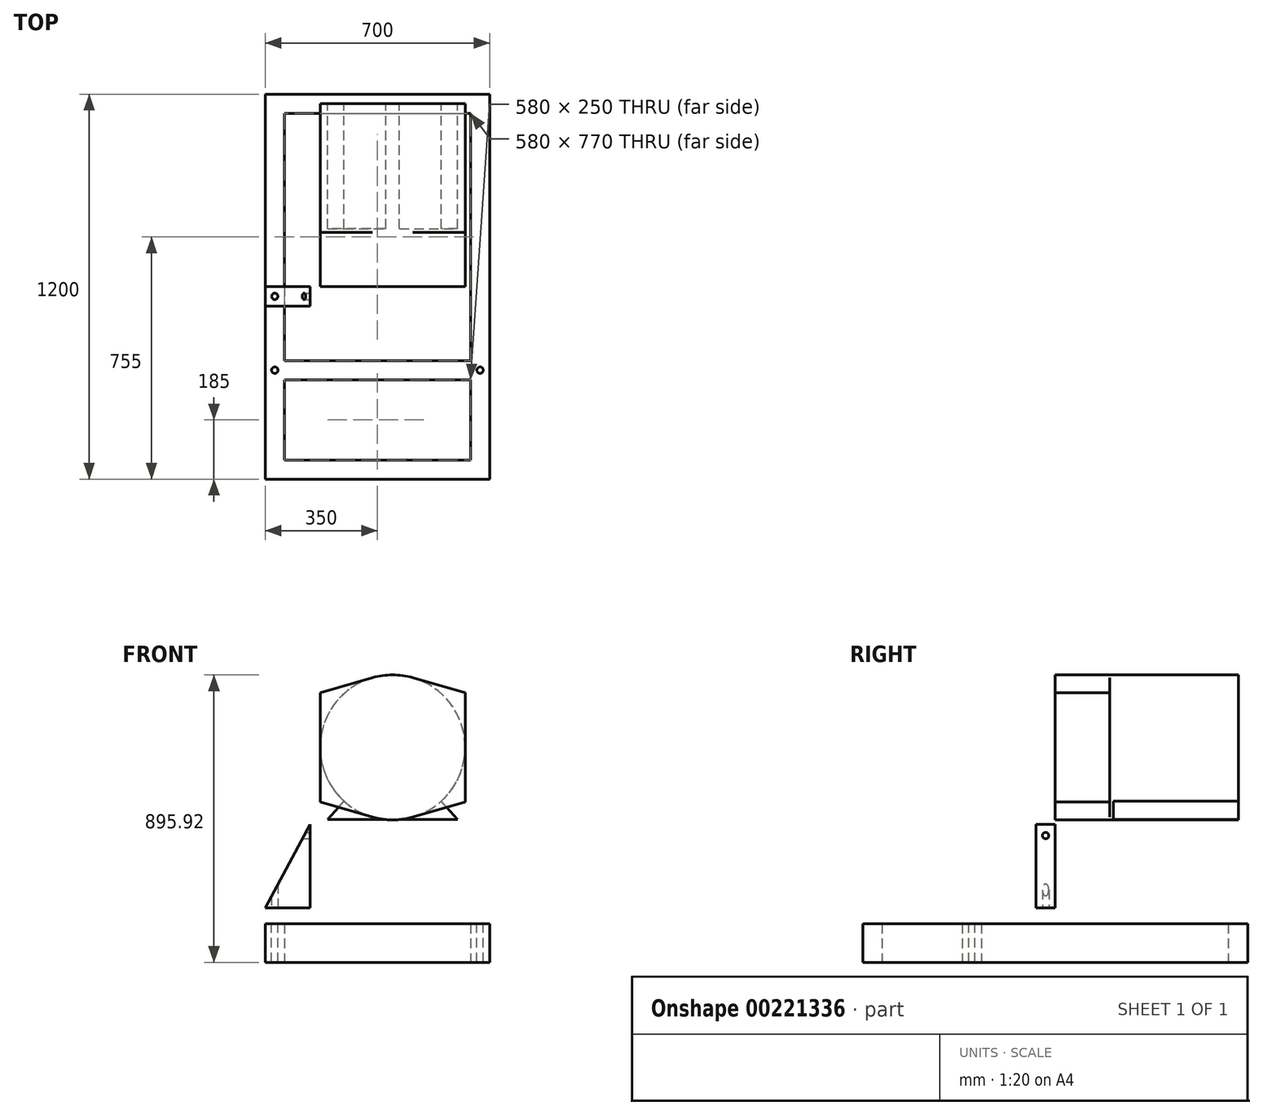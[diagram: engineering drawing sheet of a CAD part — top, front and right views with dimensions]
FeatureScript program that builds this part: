
annotation { "Feature Type Name" : "Feature", "Feature Type Description" : "" }
export const myFeature = defineFeature(function(context is Context, id is Id, definition is map)
    precondition{}
    {
        {
            var Q0;
            Q0=qCreatedBy(makeId("Top.planeOp"),FACE);
            var sketch = newSketch(context, id + "F0", { "sketchPlane" : qUnion([Q0])});
            skLineSegment(sketch, "E0.bottom", {"start": v(-300, 600) * mm, "end": v(400, 600) * mm});
            skLineSegment(sketch, "E0.top", {"start": v(-300, -600) * mm, "end": v(400, -600) * mm});
            skLineSegment(sketch, "E0.left", {"start": v(-300, 600) * mm, "end": v(-300, -600) * mm});
            skLineSegment(sketch, "E0.right", {"start": v(400, 600) * mm, "end": v(400, -600) * mm});
            skLineSegment(sketch, "E1.bottom", {"start": v(-240, 540) * mm, "end": v(340, 540) * mm});
            skLineSegment(sketch, "E1.top", {"start": v(-240, -540) * mm, "end": v(340, -540) * mm});
            skLineSegment(sketch, "E1.left", {"start": v(-240, 540) * mm, "end": v(-240, -540) * mm});
            skLineSegment(sketch, "E1.right", {"start": v(340, 540) * mm, "end": v(340, -540) * mm});
            skLineSegment(sketch, "E2", {"start": v(-240, -290) * mm, "end": v(340, -290) * mm});
            skLineSegment(sketch, "E3.0", {"start": v(-240, -230) * mm, "end": v(340, -230) * mm});
            skSolve(sketch);
        }
        {
            var Q0;
            Q0=makeQuery(id+"F0.imprint","IMPRINT",FACE,{"disambiguationData":[TD([[makeQuery(id+"F0.imprint","IMPRINT",EDGE,{"derivedFrom":sQuery(id+"F0.wireOp",EDGE,"E0.bottom")}),-1.0]])]});
            extrude(context, id + "F1", {"entities" : qUnion([Q0]), "depth" : 120 * mm});
        }
        {
            var Q0;
            {var subQ0=sQuery(id+"F0.wireOp",EDGE,"E2");Q0=makeQuery(id+"F0.imprint","IMPRINT",FACE,{"disambiguationData":[TD([[makeQuery(id+"F0.imprint","IMPRINT",EDGE,{"derivedFrom":subQ0}),1.0]])]});}
            extrude(context, id + "F2", {"entities" : qUnion([Q0]), "operationType" : NewBodyOperationType.ADD, "depth" : 120 * mm});
        }
        {
            var Q0;
            Q0=qCreatedBy(makeId("Front.planeOp"),FACE);
            var sketch = newSketch(context, id + "F3", { "sketchPlane" : qUnion([Q0])});
            skLineSegment(sketch, "E4", {"start": v(-160, 170) * mm, "end": v(-160, 430) * mm});
            skLineSegment(sketch, "E5", {"start": v(-160, 430) * mm, "end": v(-300, 170) * mm});
            skLineSegment(sketch, "E6", {"start": v(-300, 170) * mm, "end": v(-160, 170) * mm});
            skSolve(sketch);
        }
        {
            var Q0;
            Q0=makeQuery(id+"F3.imprint","IMPRINT",FACE,{"disambiguationData":[TD([[makeQuery(id+"F3.imprint","IMPRINT",EDGE,{"derivedFrom":sQuery(id+"F3.wireOp",EDGE,"E4")}),1.0]])]});
            extrude(context, id + "F4", {"entities" : qUnion([Q0]), "depth" : 60 * mm});
        }
        {
            var Q0;
            {var subQ0=sQuery(id+"F0.wireOp",EDGE,"E1.right");var subQ1=sQuery(id+"F0.wireOp",EDGE,"E1.left");Q0=makeQuery(id+"F2.boolean.opBoolean","MERGE",FACE,{"derivedFrom":[makeQuery(id+"F1.opExtrude","CAP_FACE",FACE,{"disambiguationData":[OSD([sQuery(id+"F0.wireOp",EDGE,"E0.bottom"),sQuery(id+"F0.wireOp",EDGE,"E0.top"),sQuery(id+"F0.wireOp",EDGE,"E0.left"),sQuery(id+"F0.wireOp",EDGE,"E0.right"),sQuery(id+"F0.wireOp",EDGE,"E1.bottom"),sQuery(id+"F0.wireOp",EDGE,"E1.top"),subQ1,subQ0])],"isStart":false}),makeQuery(id+"F2.opExtrude","CAP_FACE",FACE,{"disambiguationData":[OSD([subQ1,subQ0,sQuery(id+"F0.wireOp",EDGE,"E2"),sQuery(id+"F0.wireOp",EDGE,"E3.0")])],"isStart":false})]});}
            var sketch = newSketch(context, id + "F5", { "sketchPlane" : qUnion([Q0])});
            skCircle(sketch, "E7", {"center": v(-270, -260) * mm, "radius": 10 * mm});
            skCircle(sketch, "E8", {"center": v(370, -260) * mm, "radius": 10 * mm});
            skSolve(sketch);
        }
        {
            var Q0;
            Q0=makeQuery(id+"F5.imprint","IMPRINT",FACE,{"disambiguationData":[TD([[makeQuery(id+"F5.imprint","IMPRINT",EDGE,{"derivedFrom":sQuery(id+"F5.wireOp",EDGE,"E7")}),1.0]])]});
            var Q1;
            Q1=makeQuery(id+"F5.imprint","IMPRINT",FACE,{"disambiguationData":[TD([[makeQuery(id+"F5.imprint","IMPRINT",EDGE,{"derivedFrom":sQuery(id+"F5.wireOp",EDGE,"E8")}),1.0]])]});
            var Q2;
            Q2=sQuery(id+"F5.wireOp",EDGE,"E7");
            extrude(context, id + "F6", {"entities" : qUnion([Q0, Q1]), "operationType" : NewBodyOperationType.REMOVE, "surfaceEntities" : qUnion([Q2]), "oppositeDirection" : true, "depth" : 200 * mm});
        }
        {
            var Q0;
            Q0=makeQuery(id+"F4.opExtrude","SWEPT_FACE",FACE,{"disambiguationData":[OSD([sQuery(id+"F3.wireOp",EDGE,"E6")])]});
            var sketch = newSketch(context, id + "F7", { "sketchPlane" : qUnion([Q0])});
            skCircle(sketch, "E9", {"center": v(-270, 30) * mm, "radius": 10 * mm});
            skSolve(sketch);
        }
        {
            var Q0;
            Q0=makeQuery(id+"F7.imprint","IMPRINT",FACE,{"disambiguationData":[TD([[makeQuery(id+"F7.imprint","IMPRINT",EDGE,{"derivedFrom":sQuery(id+"F7.wireOp",EDGE,"E9")}),1.0]])]});
            extrude(context, id + "F8", {"entities" : qUnion([Q0]), "operationType" : NewBodyOperationType.REMOVE, "oppositeDirection" : true, "depth" : 100 * mm});
        }
        {
            var Q0;
            Q0=makeQuery(id+"F4.opExtrude","SWEPT_FACE",FACE,{"disambiguationData":[OSD([sQuery(id+"F3.wireOp",EDGE,"E4")])]});
            var sketch = newSketch(context, id + "F9", { "sketchPlane" : qUnion([Q0])});
            skCircle(sketch, "E10", {"center": v(-30, 395) * mm, "radius": 10 * mm});
            skSolve(sketch);
        }
        {
            var Q0;
            Q0=makeQuery(id+"F9.imprint","IMPRINT",FACE,{"disambiguationData":[TD([[makeQuery(id+"F9.imprint","IMPRINT",EDGE,{"derivedFrom":sQuery(id+"F9.wireOp",EDGE,"E10")}),1.0]])]});
            extrude(context, id + "F10", {"entities" : qUnion([Q0]), "operationType" : NewBodyOperationType.REMOVE, "oppositeDirection" : true, "depth" : 50 * mm});
        }
        {
            var Q0;
            Q0=qCreatedBy(makeId("Front.planeOp"),FACE);
            var sketch = newSketch(context, id + "F11", { "sketchPlane" : qUnion([Q0])});
            skCircle(sketch, "E11", {"center": v(97.42, 669.92) * mm, "radius": 226 * mm});
            skSolve(sketch);
        }
        {
            var Q0;
            Q0=makeQuery(id+"F11.imprint","IMPRINT",FACE,{"disambiguationData":[TD([[makeQuery(id+"F11.imprint","IMPRINT",EDGE,{"derivedFrom":sQuery(id+"F11.wireOp",EDGE,"E11")}),1.0]])]});
            extrude(context, id + "F12", {"entities" : qUnion([Q0]), "oppositeDirection" : true, "depth" : 571 * mm});
        }
        {
            var Q0;
            Q0=makeQuery(id+"F12.opExtrude","CAP_FACE",FACE,{"disambiguationData":[OSD([sQuery(id+"F11.wireOp",EDGE,"E11")])],"isStart":true});
            var sketch = newSketch(context, id + "F13", { "sketchPlane" : qUnion([Q0])});
            skLineSegment(sketch, "E12", {"start": v(97.42, 669.92) * mm, "end": v(323.42, 669.92) * mm});
            skLineSegment(sketch, "E13", {"start": v(97.42, 669.92) * mm, "end": v(97.42, 443.92) * mm});
            skLineSegment(sketch, "E14", {"start": v(323.42, 499.92) * mm, "end": v(160.08, 452.78) * mm});
            skLineSegment(sketch, "E15", {"start": v(323.42, 499.92) * mm, "end": v(323.42, 669.92) * mm});
            skLineSegment(sketch, "E16.MirrorCS", {"start": v(323.42, 839.92) * mm, "end": v(323.42, 669.92) * mm});
            skLineSegment(sketch, "E17.MirrorCS", {"start": v(323.42, 839.92) * mm, "end": v(160.08, 887.06) * mm});
            skLineSegment(sketch, "E18.MirrorCS", {"start": v(-128.58, 839.92) * mm, "end": v(-128.58, 669.92) * mm});
            skLineSegment(sketch, "E19.MirrorCS", {"start": v(-128.58, 839.92) * mm, "end": v(34.75, 887.06) * mm});
            skLineSegment(sketch, "E20.MirrorCS", {"start": v(-128.58, 499.92) * mm, "end": v(-128.58, 669.92) * mm});
            skLineSegment(sketch, "E21.MirrorCS", {"start": v(-128.58, 499.92) * mm, "end": v(34.75, 452.78) * mm});
            skSolve(sketch);
        }
        {
            var Q0;
            {var subQ0=sQuery(id+"F13.wireOp",EDGE,"E14");Q0=makeQuery(id+"F13.imprint","IMPRINT",FACE,{"disambiguationData":[TD([[makeQuery(id+"F13.imprint","IMPRINT",EDGE,{"derivedFrom":subQ0}),-1.0]])]});}
            var Q1;
            {var subQ0=sQuery(id+"F13.wireOp",EDGE,"E16.MirrorCS");Q1=makeQuery(id+"F13.imprint","IMPRINT",FACE,{"disambiguationData":[TD([[makeQuery(id+"F13.imprint","IMPRINT",EDGE,{"derivedFrom":subQ0}),-1.0]])]});}
            var Q2;
            {var subQ0=sQuery(id+"F13.wireOp",EDGE,"E18.MirrorCS");Q2=makeQuery(id+"F13.imprint","IMPRINT",FACE,{"disambiguationData":[TD([[makeQuery(id+"F13.imprint","IMPRINT",EDGE,{"derivedFrom":subQ0}),1.0]])]});}
            var Q3;
            {var subQ0=sQuery(id+"F13.wireOp",EDGE,"E20.MirrorCS");Q3=makeQuery(id+"F13.imprint","IMPRINT",FACE,{"disambiguationData":[TD([[makeQuery(id+"F13.imprint","IMPRINT",EDGE,{"derivedFrom":subQ0}),-1.0]])]});}
            extrude(context, id + "F14", {"entities" : qUnion([Q0, Q1, Q2, Q3]), "operationType" : NewBodyOperationType.ADD, "oppositeDirection" : true, "depth" : 170 * mm});
        }
        {
            var Q0;
            Q0=makeQuery(id+"F12.opExtrude","CAP_FACE",FACE,{"disambiguationData":[OSD([sQuery(id+"F11.wireOp",EDGE,"E11")])],"isStart":false});
            var sketch = newSketch(context, id + "F15", { "sketchPlane" : qUnion([Q0])});
            skLineSegment(sketch, "E22", {"start": v(-97.42, 669.92) * mm, "end": v(-97.42, 444.92) * mm});
            skLineSegment(sketch, "E23", {"start": v(-97.42, 444.92) * mm, "end": v(-300.42, 444.92) * mm});
            skLineSegment(sketch, "E24", {"start": v(-300.42, 444.92) * mm, "end": v(-97.42, 669.92) * mm});
            skLineSegment(sketch, "E25.MirrorCS", {"start": v(-97.42, 444.92) * mm, "end": v(105.58, 444.92) * mm});
            skLineSegment(sketch, "E26.MirrorCS", {"start": v(105.58, 444.92) * mm, "end": v(-97.42, 669.92) * mm});
            skSolve(sketch);
        }
        {
            var Q0;
            {var subQ0=sQuery(id+"F15.wireOp",EDGE,"E24");var subQ1=sQuery(id+"F15.wireOp",EDGE,"E23");var subQ2=makeQuery(id+"F15.imprint","INTERSECT",VERTEX,{"derivedFrom":[subQ1,subQ0]});Q0=makeQuery(id+"F15.imprint","IMPRINT",FACE,{"disambiguationData":[TD([[makeQuery(id+"F15.imprint","IMPRINT",EDGE,{"disambiguationData":[TD([[subQ2,1.0]])],"derivedFrom":subQ1}),-1.0]])]});}
            var Q1;
            {var subQ0=sQuery(id+"F15.wireOp",EDGE,"E26.MirrorCS");var subQ1=sQuery(id+"F15.wireOp",EDGE,"E25.MirrorCS");var subQ2=makeQuery(id+"F15.imprint","INTERSECT",VERTEX,{"derivedFrom":[subQ1,subQ0]});Q1=makeQuery(id+"F15.imprint","IMPRINT",FACE,{"disambiguationData":[TD([[makeQuery(id+"F15.imprint","IMPRINT",EDGE,{"disambiguationData":[TD([[subQ2,1.0]])],"derivedFrom":subQ1}),1.0]])]});}
            extrude(context, id + "F16", {"entities" : qUnion([Q0, Q1]), "operationType" : NewBodyOperationType.ADD, "oppositeDirection" : true, "depth" : 390 * mm});
        }
    });
